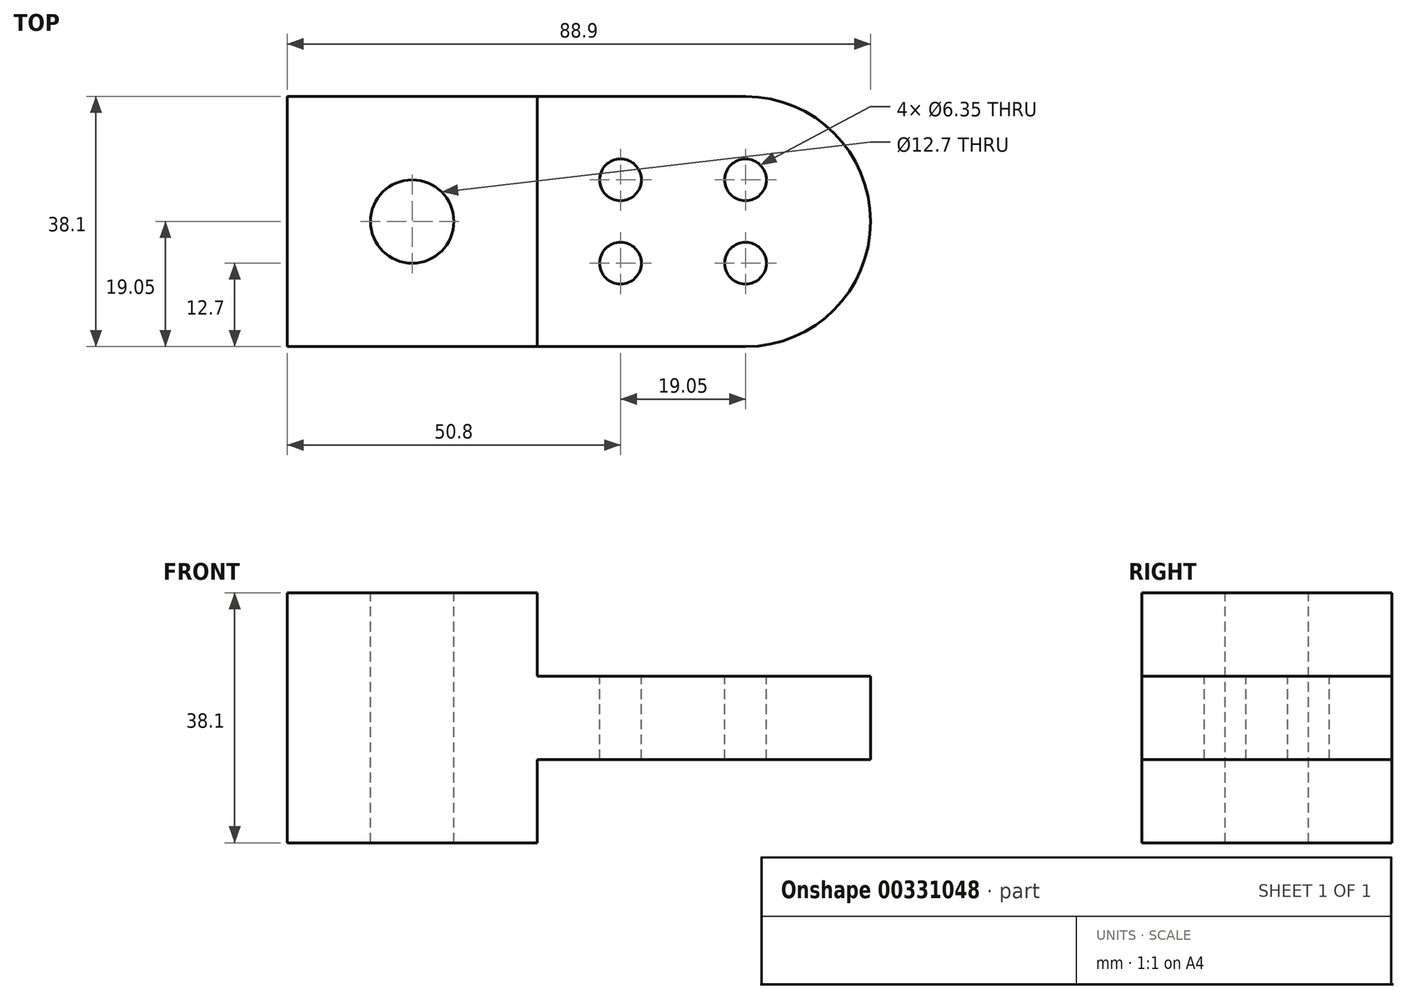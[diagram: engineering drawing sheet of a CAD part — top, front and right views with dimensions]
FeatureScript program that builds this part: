
annotation { "Feature Type Name" : "Feature", "Feature Type Description" : "" }
export const myFeature = defineFeature(function(context is Context, id is Id, definition is map)
    precondition{}
    {
        {
            var Q0;
            Q0=qCreatedBy(makeId("Front.planeOp"),FACE);
            var sketch = newSketch(context, id + "F0", { "sketchPlane" : qUnion([Q0])});
            skLineSegment(sketch, "E0", {"start": v(0, 0) * mm, "end": v(0, 38.1) * mm});
            skLineSegment(sketch, "E1", {"start": v(0, 38.1) * mm, "end": v(38.1, 38.1) * mm});
            skLineSegment(sketch, "E2", {"start": v(38.1, 38.1) * mm, "end": v(38.1, 25.4) * mm});
            skLineSegment(sketch, "E3", {"start": v(38.1, 25.4) * mm, "end": v(88.9, 25.4) * mm});
            skLineSegment(sketch, "E4", {"start": v(88.9, 25.4) * mm, "end": v(88.9, 12.7) * mm});
            skLineSegment(sketch, "E5", {"start": v(88.9, 12.7) * mm, "end": v(38.1, 12.7) * mm});
            skLineSegment(sketch, "E6", {"start": v(38.1, 12.7) * mm, "end": v(38.1, 0) * mm});
            skLineSegment(sketch, "E7", {"start": v(38.1, 0) * mm, "end": v(0, 0) * mm});
            skSolve(sketch);
        }
        {
            var Q0;
            Q0 = qSketchRegion(id + "F0", true);
            extrude(context, id + "F1", {"entities" : qUnion([Q0]), "depth" : 38.1 * mm});
        }
        {
            var Q0;
            Q0=makeQuery(id+"F1.opExtrude","SWEPT_FACE",FACE,{"disambiguationData":[OSD([sQuery(id+"F0.wireOp",EDGE,"E3")])]});
            var sketch = newSketch(context, id + "F2", { "sketchPlane" : qUnion([Q0])});
            skLineSegment(sketch, "E8.0.0", {"start": v(88.9, 0) * mm, "end": v(38.1, 0) * mm});
            skLineSegment(sketch, "E8.0.1", {"start": v(38.1, 0) * mm, "end": v(38.1, -38.1) * mm});
            skLineSegment(sketch, "E8.0.2", {"start": v(38.1, -38.1) * mm, "end": v(88.9, -38.1) * mm});
            skLineSegment(sketch, "E8.0.3", {"start": v(88.9, -38.1) * mm, "end": v(88.9, 0) * mm});
            skArc(sketch, "E9", {"start": v(69.85, -38.1) * mm, "mid": v(88.9, -19.05) * mm, "end": v(69.85, 0) * mm});
            skSolve(sketch);
        }
        {
            var Q0;
            {var subQ0=sQuery(id+"F2.wireOp",EDGE,"E8.0.3");var subQ1=sQuery(id+"F2.wireOp",EDGE,"E8.0.0");var subQ2=makeQuery(id+"F2.imprint","INTERSECT",VERTEX,{"derivedFrom":[subQ1,subQ0]});Q0=makeQuery(id+"F2.imprint","IMPRINT",FACE,{"disambiguationData":[TD([[makeQuery(id+"F2.imprint","IMPRINT",EDGE,{"disambiguationData":[TD([[subQ2,1.0]])],"derivedFrom":subQ1}),-1.0]])]});}
            var Q1;
            {var subQ0=sQuery(id+"F2.wireOp",EDGE,"E8.0.3");var subQ1=sQuery(id+"F2.wireOp",EDGE,"E8.0.2");var subQ2=makeQuery(id+"F2.imprint","INTERSECT",VERTEX,{"derivedFrom":[subQ1,subQ0]});Q1=makeQuery(id+"F2.imprint","IMPRINT",FACE,{"disambiguationData":[TD([[makeQuery(id+"F2.imprint","IMPRINT",EDGE,{"disambiguationData":[TD([[subQ2,1.0]])],"derivedFrom":subQ1}),1.0]])]});}
            extrude(context, id + "F3", {"entities" : qUnion([Q0, Q1]), "operationType" : NewBodyOperationType.REMOVE, "oppositeDirection" : true, "depth" : 25.4 * mm});
        }
        {
            var Q0;
            Q0=makeQuery(id+"F1.opExtrude","SWEPT_FACE",FACE,{"disambiguationData":[OSD([sQuery(id+"F0.wireOp",EDGE,"E1")])]});
            var sketch = newSketch(context, id + "F4", { "sketchPlane" : qUnion([Q0])});
            skCircle(sketch, "E10", {"center": v(19.05, -19.05) * mm, "radius": 6.35 * mm});
            skSolve(sketch);
        }
        {
            var Q0;
            Q0 = qSketchRegion(id + "F4", true);
            extrude(context, id + "F5", {"entities" : qUnion([Q0]), "operationType" : NewBodyOperationType.REMOVE, "oppositeDirection" : true, "depth" : 38.1 * mm});
        }
        {
            var Q0;
            Q0=makeQuery(id+"F1.opExtrude","SWEPT_FACE",FACE,{"disambiguationData":[OSD([sQuery(id+"F0.wireOp",EDGE,"E3")])]});
            var sketch = newSketch(context, id + "F6", { "sketchPlane" : qUnion([Q0])});
            skCircle(sketch, "E11", {"center": v(50.8, -12.7) * mm, "radius": 3.18 * mm});
            skCircle(sketch, "E12", {"center": v(50.8, -25.4) * mm, "radius": 3.18 * mm});
            skCircle(sketch, "E13", {"center": v(69.85, -25.4) * mm, "radius": 3.18 * mm});
            skCircle(sketch, "E14", {"center": v(69.85, -12.7) * mm, "radius": 3.18 * mm});
            skSolve(sketch);
        }
        {
            var Q0;
            Q0 = qSketchRegion(id + "F6", true);
            extrude(context, id + "F7", {"entities" : qUnion([Q0]), "operationType" : NewBodyOperationType.REMOVE, "oppositeDirection" : true, "depth" : 25.4 * mm});
        }
    });
